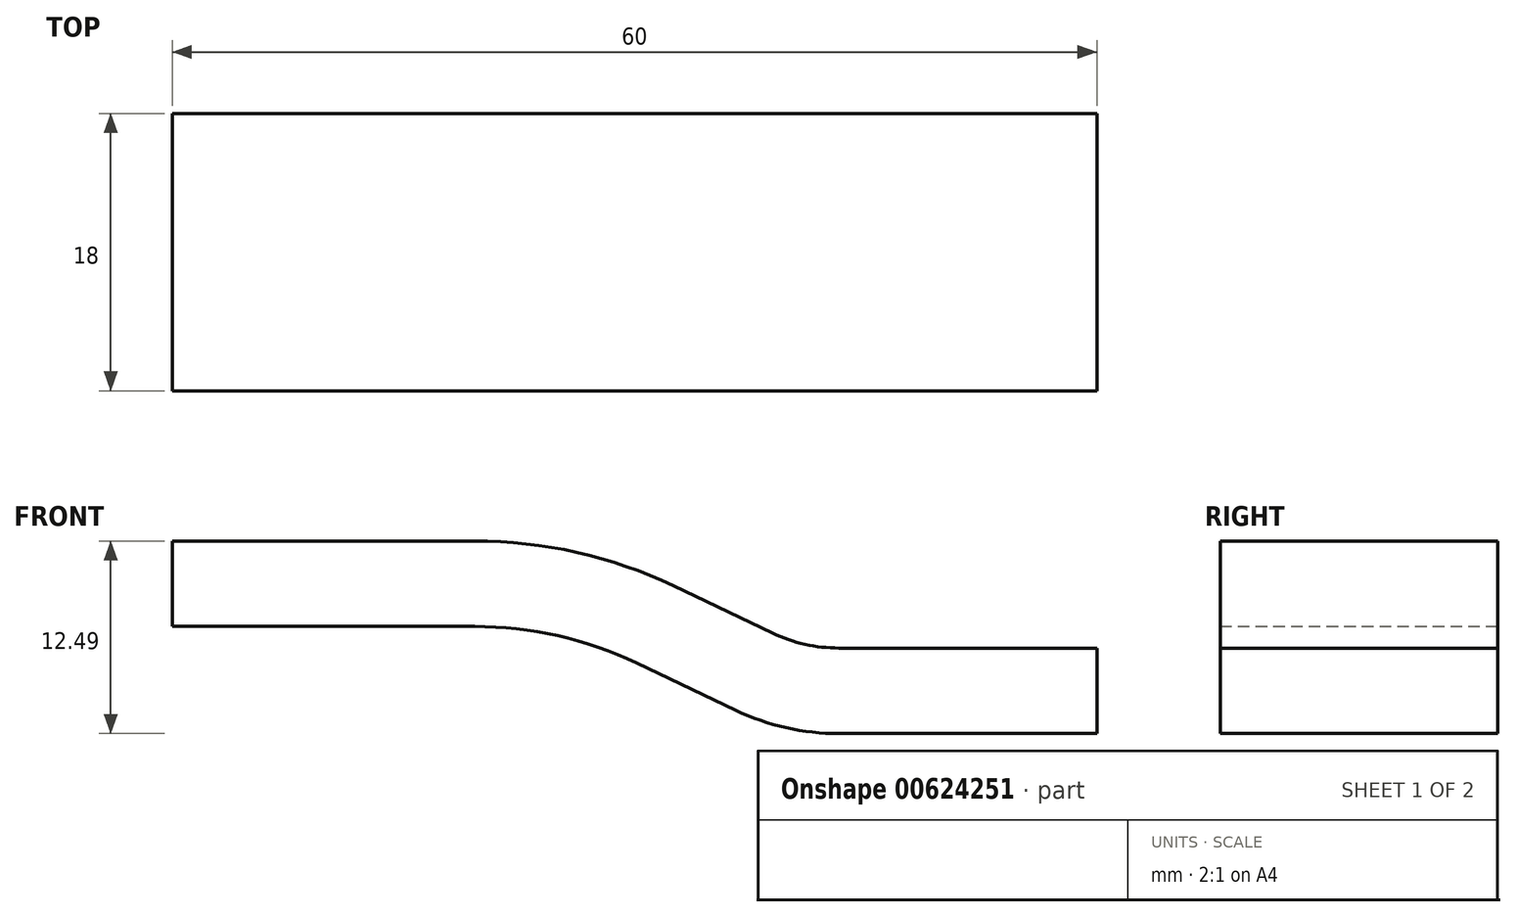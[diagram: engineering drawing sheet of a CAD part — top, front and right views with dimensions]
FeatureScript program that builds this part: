
annotation { "Feature Type Name" : "Feature", "Feature Type Description" : "" }
export const myFeature = defineFeature(function(context is Context, id is Id, definition is map)
    precondition{}
    {
        {
            var Q0;
            Q0=qCreatedBy(makeId("Front.planeOp"),FACE);
            var sketch = newSketch(context, id + "F0", { "sketchPlane" : qUnion([Q0])});
            skLineSegment(sketch, "E0", {"start": v(-30, 0) * mm, "end": v(30, 0) * mm, "construction": true});
            skLineSegment(sketch, "E1", {"start": v(-30, 9.73) * mm, "end": v(-10.38, 9.73) * mm});
            skLineSegment(sketch, "E2", {"start": v(2.52, 6.81) * mm, "end": v(8.96, 3.75) * mm});
            skLineSegment(sketch, "E3", {"start": v(13.26, 2.77) * mm, "end": v(30, 2.77) * mm});
            skLineSegment(sketch, "E4", {"start": v(30, 2.77) * mm, "end": v(30, -2.77) * mm});
            skLineSegment(sketch, "E5", {"start": v(-30, 9.73) * mm, "end": v(-30, 4.18) * mm});
            skPoint(sketch, "E6.visualSharp", {"position": v(-3.6, 9.73) * mm});
            skArc(sketch, "E6.filletArc", {"start": v(2.52, 6.81) * mm, "mid": v(-3.77, 8.99) * mm, "end": v(-10.38, 9.73) * mm});
            skPoint(sketch, "E7.visualSharp", {"position": v(11, 2.78) * mm});
            skArc(sketch, "E7.filletArc", {"start": v(8.96, 3.75) * mm, "mid": v(11.06, 3.02) * mm, "end": v(13.26, 2.77) * mm});
            skLineSegment(sketch, "E8.0", {"start": v(-30, 4.18) * mm, "end": v(-10.38, 4.18) * mm});
            skArc(sketch, "E9.0", {"start": v(0.13, 1.8) * mm, "mid": v(-4.99, 3.57) * mm, "end": v(-10.38, 4.17) * mm});
            skLineSegment(sketch, "E9.1", {"start": v(0.13, 1.8) * mm, "end": v(6.58, -1.27) * mm});
            skArc(sketch, "E9.2", {"start": v(6.58, -1.27) * mm, "mid": v(9.83, -2.4) * mm, "end": v(13.26, -2.77) * mm});
            skLineSegment(sketch, "E9.3", {"start": v(13.26, -2.77) * mm, "end": v(30, -2.77) * mm});
            skSolve(sketch);
        }
        {
            var Q0;
            Q0 = qSketchRegion(id + "F0", true);
            extrude(context, id + "F1", {"entities" : qUnion([Q0]), "depth" : 18 * mm, "offsetDistance" : 25 * mm});
        }
    });
